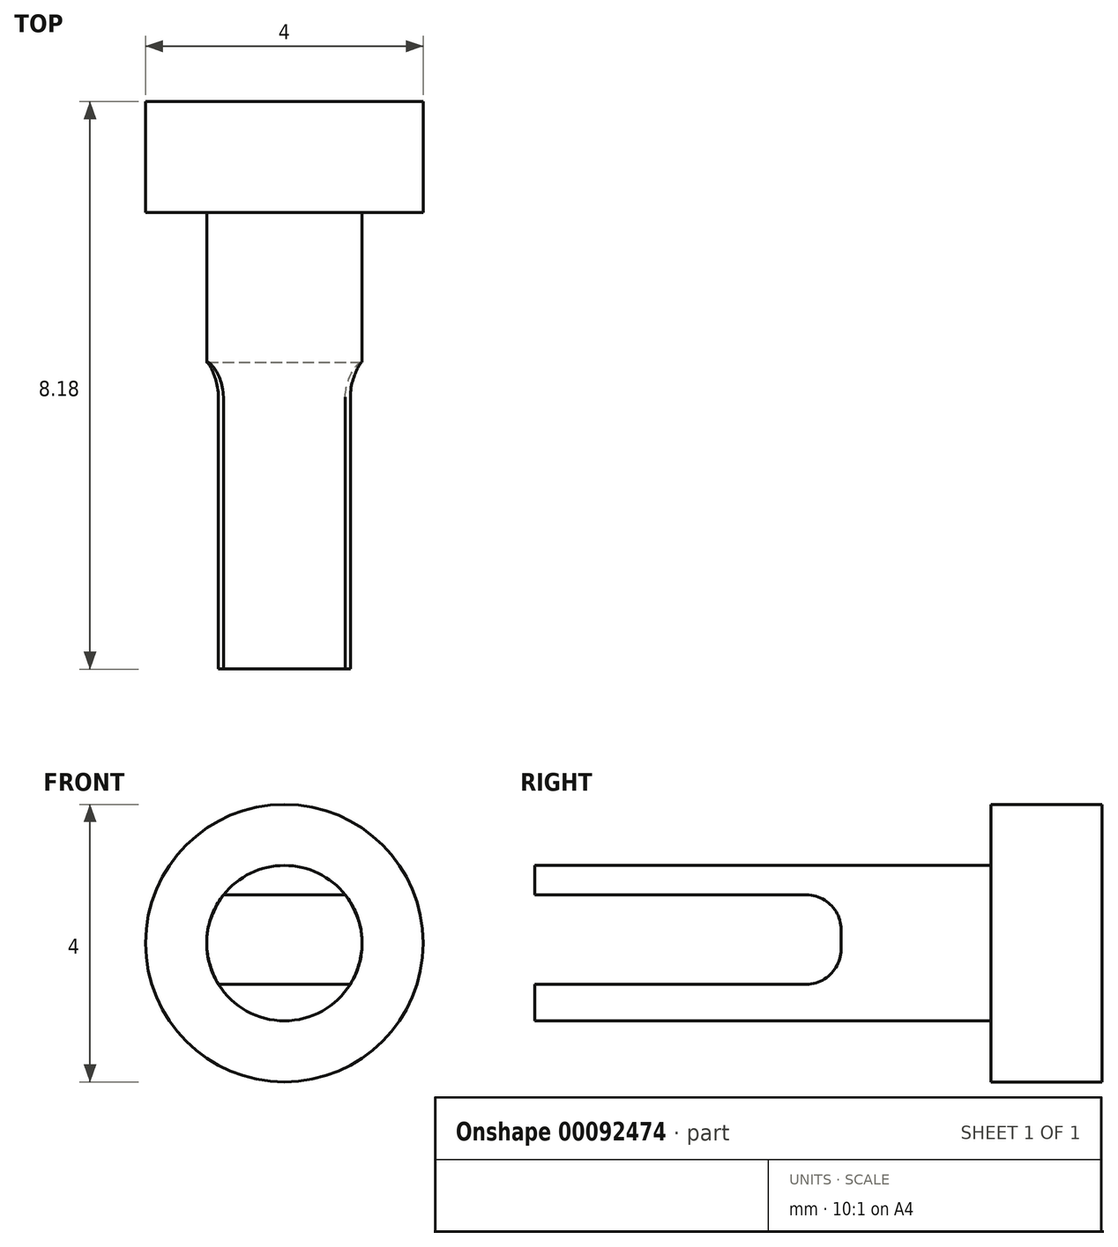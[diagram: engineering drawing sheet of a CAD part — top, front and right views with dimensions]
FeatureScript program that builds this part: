
annotation { "Feature Type Name" : "Feature", "Feature Type Description" : "" }
export const myFeature = defineFeature(function(context is Context, id is Id, definition is map)
    precondition{}
    {
        {
            var Q0;
            Q0=qCreatedBy(makeId("Right.planeOp"),FACE);
            var sketch = newSketch(context, id + "F0", { "sketchPlane" : qUnion([Q0])});
            skLineSegment(sketch, "E0.bottom", {"start": v(-0.8, -2) * mm, "end": v(0.8, -2) * mm});
            skLineSegment(sketch, "E0.top", {"start": v(-0.8, 2) * mm, "end": v(0.8, 2) * mm});
            skLineSegment(sketch, "E0.left", {"start": v(-0.8, -2) * mm, "end": v(-0.8, 2) * mm});
            skLineSegment(sketch, "E0.right", {"start": v(0.8, -2) * mm, "end": v(0.8, 2) * mm});
            skPoint(sketch, "E0.middle", {"position": v(0, 0) * mm});
            skLineSegment(sketch, "E1", {"start": v(-0.8, 1.12) * mm, "end": v(-7.38, 1.12) * mm});
            skLineSegment(sketch, "E2", {"start": v(-7.38, -1.08) * mm, "end": v(-0.8, -1.08) * mm});
            skLineSegment(sketch, "E3", {"start": v(-7.38, 1.12) * mm, "end": v(-7.38, -1.08) * mm});
            skLineSegment(sketch, "E4", {"start": v(-7.38, 1.12) * mm, "end": v(-6.8, 1.12) * mm});
            skLineSegment(sketch, "E5", {"start": v(-6.8, 1.12) * mm, "end": v(-6.8, 1.74) * mm});
            skLineSegment(sketch, "E6", {"start": v(-6.8, 1.74) * mm, "end": v(-7.38, 1.12) * mm});
            skLineSegment(sketch, "E7", {"start": v(2.32, 0) * mm, "end": v(-7.98, 0) * mm});
            skPoint(sketch, "E7.endSnap0", {"position": v(0.8, 0) * mm});
            skSolve(sketch);
        }
        {
            var Q0;
            Q0=makeQuery(id+"F0.imprint","IMPRINT",FACE,{"disambiguationData":[TD([[makeQuery(id+"F0.imprint","IMPRINT",EDGE,{"derivedFrom":sQuery(id+"F0.wireOp",EDGE,"E4")}),1.0]])]});
            var Q1;
            {var subQ6=sQuery(id+"F0.wireOp",EDGE,"E1");Q1=makeQuery(id+"F0.imprint","IMPRINT",FACE,{"disambiguationData":[TD([[makeQuery(id+"F0.imprint","IMPRINT",EDGE,{"derivedFrom":subQ6}),1.0]])]});}
            var Q2;
            {var subQ1=sQuery(id+"F0.wireOp",EDGE,"E0.top");Q2=makeQuery(id+"F0.imprint","IMPRINT",FACE,{"disambiguationData":[TD([[makeQuery(id+"F0.imprint","IMPRINT",EDGE,{"derivedFrom":subQ1}),-1.0]])]});}
            var Q3;
            Q3=sQuery(id+"F0.wireOp",EDGE,"E7");
            revolve(context, id + "F1", {"entities" : qUnion([Q0, Q1, Q2]), "axis" : qUnion([Q3]), "revolveType" : RevolveType.FULL});
        }
        {
            var Q0;
            Q0=qCreatedBy(makeId("Right.planeOp"),FACE);
            var sketch = newSketch(context, id + "F2", { "sketchPlane" : qUnion([Q0])});
            skLineSegment(sketch, "E8.bottom", {"start": v(-7.46, 0.7) * mm, "end": v(-2.96, 0.7) * mm});
            skLineSegment(sketch, "E8.top", {"start": v(-7.46, -0.6) * mm, "end": v(-2.96, -0.6) * mm});
            skLineSegment(sketch, "E8.left", {"start": v(-7.46, 0.7) * mm, "end": v(-7.46, -0.6) * mm});
            skLineSegment(sketch, "E8.right", {"start": v(-2.96, 0.7) * mm, "end": v(-2.96, -0.6) * mm});
            skSolve(sketch);
        }
        {
            var Q0;
            Q0 = qSketchRegion(id + "F2", true);
            extrude(context, id + "F3", {"entities" : qUnion([Q0]), "operationType" : NewBodyOperationType.REMOVE, "oppositeDirection" : true, "depth" : 25 * mm, "symmetric" : true});
        }
        {
            var Q0;
            Q0=makeQuery(id+"F3.boolean.opBoolean","COPY",EDGE,{"derivedFrom":makeQuery(id+"F3.opExtrude","SWEPT_EDGE",EDGE,{"disambiguationData":[OSD([sQuery(id+"F2.wireOp",EDGE,"E8.top"),sQuery(id+"F2.wireOp",EDGE,"E8.right")])]})});
            var Q1;
            Q1=makeQuery(id+"F3.boolean.opBoolean","COPY",EDGE,{"derivedFrom":makeQuery(id+"F3.opExtrude","SWEPT_EDGE",EDGE,{"disambiguationData":[OSD([sQuery(id+"F2.wireOp",EDGE,"E8.bottom"),sQuery(id+"F2.wireOp",EDGE,"E8.right")])]})});
            fillet(context, id + "F4", {"entities" : qUnion([Q0, Q1]), "radius" : .5 * mm, "tangentPropagation" : true, "allowEdgeOverflow" : false});
        }
    });
